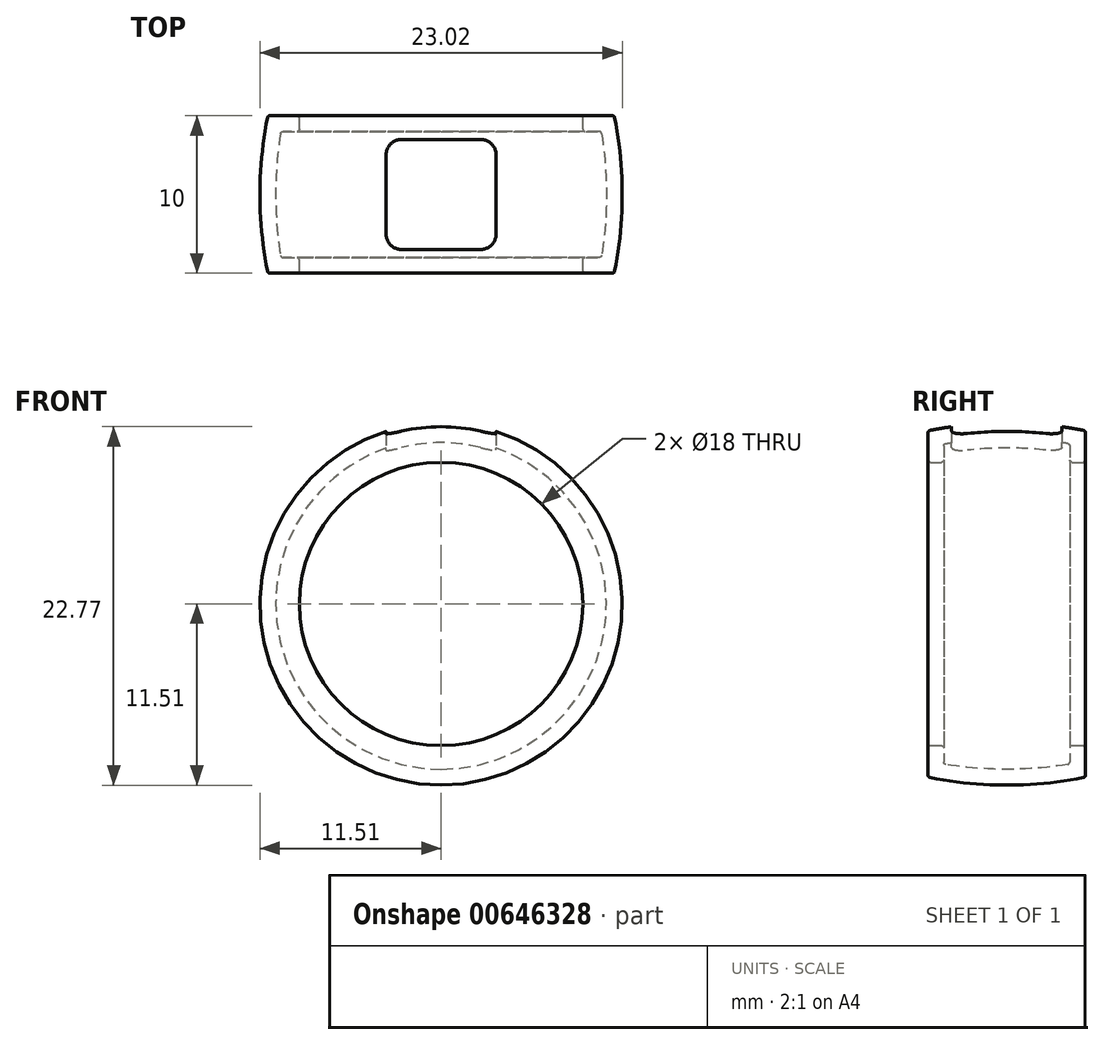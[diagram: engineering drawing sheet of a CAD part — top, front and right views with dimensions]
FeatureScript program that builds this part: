
annotation { "Feature Type Name" : "Feature", "Feature Type Description" : "" }
export const myFeature = defineFeature(function(context is Context, id is Id, definition is map)
    precondition{}
    {
        {
            var Q0;
            Q0=qCreatedBy(makeId("Top.planeOp"),FACE);
            var sketch = newSketch(context, id + "F0", { "sketchPlane" : qUnion([Q0])});
            skLineSegment(sketch, "E0", {"start": v(0, 0) * mm, "end": v(-9, 0) * mm, "construction": true});
            skLineSegment(sketch, "E1", {"start": v(-9, 5) * mm, "end": v(-9, -5) * mm});
            skLineSegment(sketch, "E2", {"start": v(-9, 5) * mm, "end": v(-11, 5) * mm});
            skLineSegment(sketch, "E3", {"start": v(-9, -5) * mm, "end": v(-11, -5) * mm});
            skArc(sketch, "E4", {"start": v(-11, 5) * mm, "mid": v(-11.5, 0) * mm, "end": v(-11, -5) * mm});
            skLineSegment(sketch, "E5", {"start": v(0, 0) * mm, "end": v(0, -9.73) * mm, "construction": true});
            skSolve(sketch);
        }
        {
            var Q0;
            Q0=makeQuery(id+"F0.imprint","IMPRINT",FACE,{"disambiguationData":[TD([[makeQuery(id+"F0.imprint","IMPRINT",EDGE,{"derivedFrom":sQuery(id+"F0.wireOp",EDGE,"E1")}),-1.0]])]});
            var Q1;
            Q1=sQuery(id+"F0.wireOp",EDGE,"E5");
            revolve(context, id + "F1", {"entities" : qUnion([Q0]), "axis" : qUnion([Q1]), "revolveType" : RevolveType.FULL});
        }
        {
            var Q0;
            Q0=makeQuery(id+"F1.opRevolve","SWEPT_FACE",FACE,{"disambiguationData":[OSD([sQuery(id+"F0.wireOp",EDGE,"E1")])]});
            shell(context, id + "F2", {"entities" : qUnion([Q0]), "thickness" : 1 * mm});
        }
        {
            var Q0;
            Q0=makeQuery(id+"F1.opRevolve","SWEPT_EDGE",EDGE,{"disambiguationData":[OSD([sQuery(id+"F0.wireOp",EDGE,"E1"),sQuery(id+"F0.wireOp",EDGE,"E3")])]});
            var Q1;
            Q1=makeQuery(id+"F2.opShell","OFFSET_FACE",FACE,{"disambiguationData":[OSD([sQuery(id+"F0.wireOp",EDGE,"E2")])]});
            var Q2;
            Q2=makeQuery(id+"F2.opShell","OFFSET_EDGE",EDGE,{"disambiguationData":[OSD([sQuery(id+"F0.wireOp",EDGE,"E1"),sQuery(id+"F0.wireOp",EDGE,"E2")])]});
            var Q3;
            Q3=makeQuery(id+"F1.opRevolve","SWEPT_FACE",FACE,{"disambiguationData":[OSD([sQuery(id+"F0.wireOp",EDGE,"E2")])]});
            var Q4;
            Q4=makeQuery(id+"F2.opShell","OFFSET_EDGE",EDGE,{"disambiguationData":[OSD([sQuery(id+"F0.wireOp",EDGE,"E1"),sQuery(id+"F0.wireOp",EDGE,"E3")])]});
            var Q5;
            Q5=makeQuery(id+"F1.opRevolve","SWEPT_FACE",FACE,{"disambiguationData":[OSD([sQuery(id+"F0.wireOp",EDGE,"E3")])]});
            var Q6;
            Q6=makeQuery(id+"F1.opRevolve","SWEPT_EDGE",EDGE,{"disambiguationData":[OSD([sQuery(id+"F0.wireOp",EDGE,"E2"),sQuery(id+"F0.wireOp",EDGE,"E4")])]});
            var Q7;
            Q7=makeQuery(id+"F2.opShell","OFFSET_EDGE",EDGE,{"disambiguationData":[OSD([sQuery(id+"F0.wireOp",EDGE,"E2"),sQuery(id+"F0.wireOp",EDGE,"E4")])]});
            var Q8;
            Q8=makeQuery(id+"F2.opShell","OFFSET_FACE",FACE,{"disambiguationData":[OSD([sQuery(id+"F0.wireOp",EDGE,"E3")])]});
            var Q9;
            Q9=makeQuery(id+"F2.opShell","OFFSET_FACE",FACE,{"disambiguationData":[OSD([sQuery(id+"F0.wireOp",EDGE,"E4")])]});
            var Q10;
            Q10=makeQuery(id+"F1.opRevolve","SWEPT_FACE",FACE,{"disambiguationData":[OSD([sQuery(id+"F0.wireOp",EDGE,"E4")])]});
            var Q11;
            Q11=makeQuery(id+"F1.opRevolve","SWEPT_EDGE",EDGE,{"disambiguationData":[OSD([sQuery(id+"F0.wireOp",EDGE,"E1"),sQuery(id+"F0.wireOp",EDGE,"E2")])]});
            var Q12;
            Q12=makeQuery(id+"F1.opRevolve","SWEPT_EDGE",EDGE,{"disambiguationData":[OSD([sQuery(id+"F0.wireOp",EDGE,"E3"),sQuery(id+"F0.wireOp",EDGE,"E4")])]});
            var Q13;
            Q13=makeQuery(id+"F1.opRevolve","SWEPT_FACE",FACE,{"disambiguationData":[OSD([sQuery(id+"F0.wireOp",EDGE,"E1")])]});
            var Q14;
            Q14=makeQuery(id+"F2.opShell","OFFSET_FACE",FACE,{"disambiguationData":[OSD([sQuery(id+"F0.wireOp",EDGE,"E1")])]});
            var Q15;
            Q15=makeQuery(id+"F2.opShell","OFFSET_EDGE",EDGE,{"disambiguationData":[OSD([sQuery(id+"F0.wireOp",EDGE,"E3"),sQuery(id+"F0.wireOp",EDGE,"E4")])]});
            fillet(context, id + "F3", {"entities" : qUnion([Q0, Q1, Q2, Q3, Q4, Q5, Q6, Q7, Q8, Q9, Q10, Q11, Q12, Q13, Q14, Q15]), "radius" : 0.15 * mm, "tangentPropagation" : true, "allowEdgeOverflow" : false});
        }
        {
            var Q0;
            Q0=qCreatedBy(makeId("Top.planeOp"),FACE);
            var sketch = newSketch(context, id + "F4", { "sketchPlane" : qUnion([Q0])});
            skPoint(sketch, "E6.middle", {"position": v(0, 0) * mm});
            skLineSegment(sketch, "E7.bottom", {"start": v(2.5, -3.5) * mm, "end": v(-2.5, -3.5) * mm});
            skLineSegment(sketch, "E7.top", {"start": v(2.5, 3.5) * mm, "end": v(-2.5, 3.5) * mm});
            skLineSegment(sketch, "E7.left", {"start": v(3.5, -2.5) * mm, "end": v(3.5, 2.5) * mm});
            skLineSegment(sketch, "E7.right", {"start": v(-3.5, -2.5) * mm, "end": v(-3.5, 2.5) * mm});
            skPoint(sketch, "E8.visualSharp", {"position": v(-3.5, 3.5) * mm});
            skArc(sketch, "E8.filletArc", {"start": v(-2.5, 3.5) * mm, "mid": v(-3.2, 3.2) * mm, "end": v(-3.5, 2.5) * mm});
            skPoint(sketch, "E9.visualSharp", {"position": v(3.5, 3.5) * mm});
            skArc(sketch, "E9.filletArc", {"start": v(3.5, 2.5) * mm, "mid": v(3.2, 3.2) * mm, "end": v(2.5, 3.5) * mm});
            skPoint(sketch, "E10.visualSharp", {"position": v(3.5, -3.5) * mm});
            skArc(sketch, "E10.filletArc", {"start": v(2.5, -3.5) * mm, "mid": v(3.2, -3.2) * mm, "end": v(3.5, -2.5) * mm});
            skPoint(sketch, "E11.visualSharp", {"position": v(-3.5, -3.5) * mm});
            skArc(sketch, "E11.filletArc", {"start": v(-3.5, -2.5) * mm, "mid": v(-3.2, -3.2) * mm, "end": v(-2.5, -3.5) * mm});
            skSolve(sketch);
        }
        {
            var Q0;
            Q0 = qSketchRegion(id + "F4", true);
            extrude(context, id + "F5", {"entities" : qUnion([Q0]), "operationType" : NewBodyOperationType.REMOVE, "endBound" : BoundingType.THROUGH_ALL, "depth" : 25 * mm, "offsetDistance" : 25 * mm});
        }
    });
